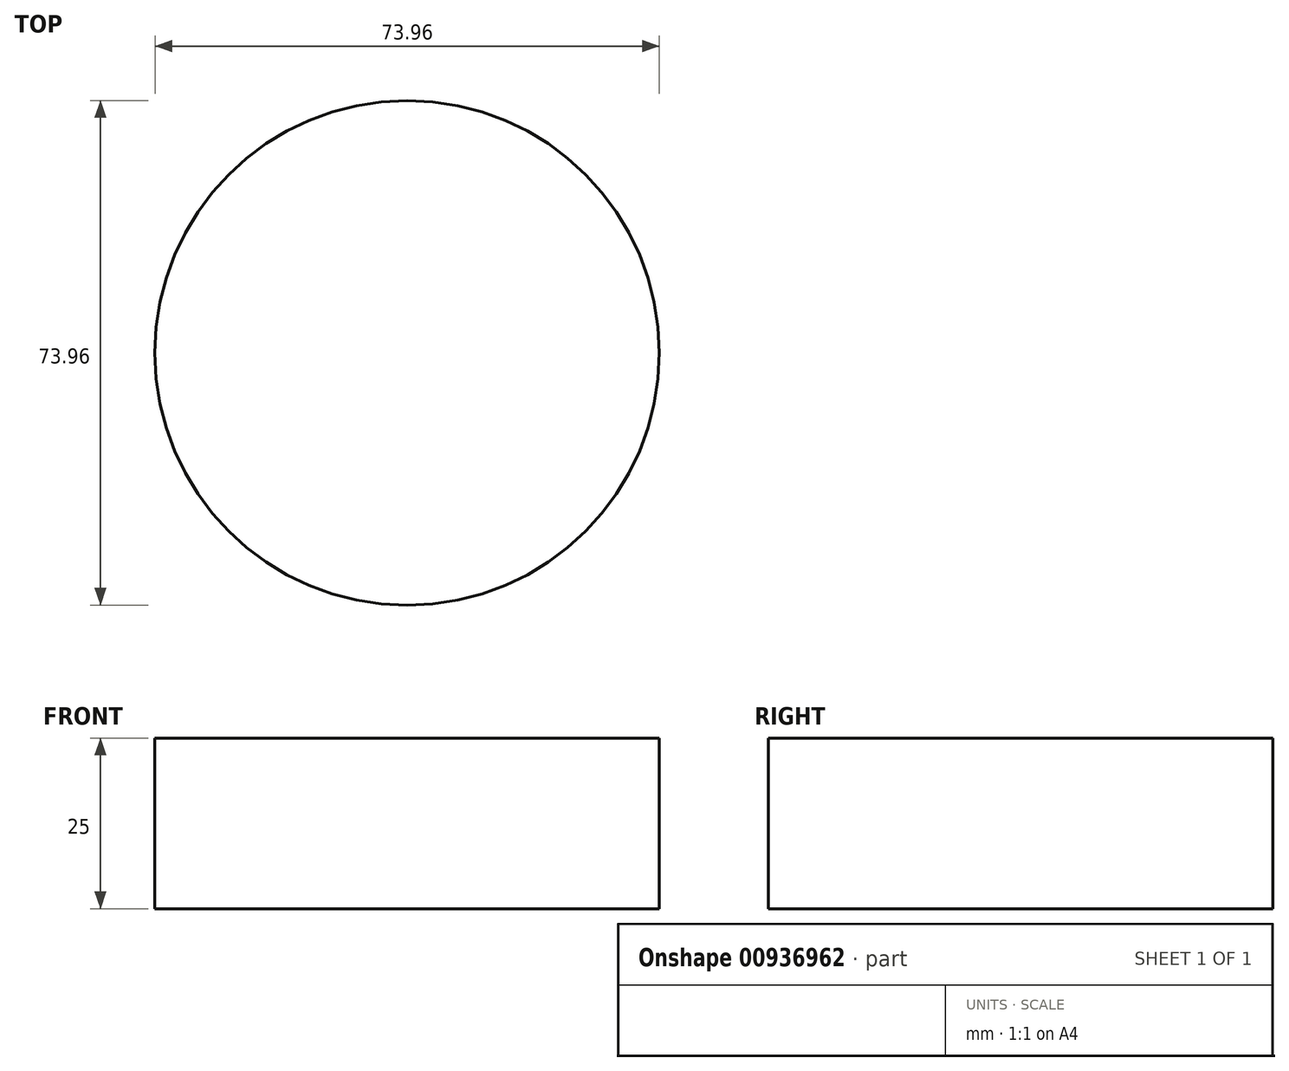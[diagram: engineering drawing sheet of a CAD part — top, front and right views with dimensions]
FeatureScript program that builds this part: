
annotation { "Feature Type Name" : "Feature", "Feature Type Description" : "" }
export const myFeature = defineFeature(function(context is Context, id is Id, definition is map)
    precondition{}
    {
        {
            var Q0;
            Q0=qCreatedBy(makeId("Top.planeOp"),FACE);
            var sketch = newSketch(context, id + "F0", { "sketchPlane" : qUnion([Q0])});
            skCircle(sketch, "E0", {"center": v(0, 0) * mm, "radius": 36.98 * mm});
            skSolve(sketch);
        }
        {
            var Q0;
            Q0=makeQuery(id+"F0.imprint","IMPRINT",FACE,{"disambiguationData":[TD([[makeQuery(id+"F0.imprint","IMPRINT",EDGE,{"derivedFrom":sQuery(id+"F0.wireOp",EDGE,"E0")}),1.0]])]});
            extrude(context, id + "F1", {"entities" : qUnion([Q0]), "depth" : 25 * mm, "offsetDistance" : 25 * mm});
        }
    });
